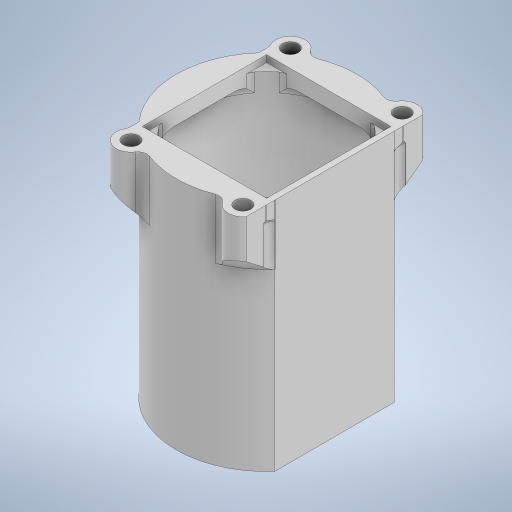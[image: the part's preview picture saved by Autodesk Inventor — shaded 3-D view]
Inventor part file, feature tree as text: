
AUTODESK INVENTOR PART (.ipt)
format: ipt  version: 2024 (Build 280153000, 153)  size: 606,720 bytes
history: native  units: in
note: dims shown in document units (in); Inventor stores cm internally (conversion verified against a paired STEP export)
features: extrude x12, projected_geometry x7, sketch x6, fillet x4, chamfer x1
ambient origin geometry x8: Origin, YZ Plane, XZ Plane, XY Plane, X Axis, Y Axis, Z Axis, Center Point
bodies: Solid1 (feature_tree)
feature tree (30):
  extrude  "Extrusion1"  Depth=1.5748in
  extrude  "Extrusion2"  Depth=1.0236in
  extrude  "Extrusion3"  Depth=0.1181in
  sketch  "Sketch4"  dims[d8=1.7106in d9=0.0in d10=0.1378in]
  extrude  "Extrusion4"  Depth=0.1378in
  extrude  "Extrusion5"  Depth=0.9744in
  extrude  "Extrusion6"  Depth=0.4872in
  extrude  "Extrusion7"  Depth=0.6939in
  extrude  "Extrusion8"  Depth=0.2559in
  fillet  "Fillet1"  Radius=1.1811in
  extrude  "Extrusion9"  Depth=0.5906in
  chamfer  "Chamfer1"  Distance=0.5906in
  fillet  "Fillet4"  Radius=0.2362in
  fillet  "Fillet5"  Radius=0.2362in
  fillet  "Fillet6"  Radius=0.0492in
  extrude  "Extrusion10"  Depth=1.3878in
  extrude  "Extrusion11"  Depth=0.0787in TaperAngle=0.0deg
  extrude  "Extrusion12"  Depth=0.0591in TaperAngle=0.0deg
  sketch  "Sketch1"  dims[d0=0.878in d1=1.5748in]
  sketch  "Sketch2"  dims[d2=0.1181in d3=0.0in d4=1.0236in]
  sketch  "Sketch3"  dims[d5=0.1575in d6=0.0in d7=0.1181in]
  projected_geometry  "Projected Loop1"
  projected_geometry  "Projected Loop2"
  sketch  "Sketch5"  dims[d14=1.3878in d15=0.9744in]
  projected_geometry  "Projected Loop3"
  projected_geometry  "Projected Loop4"
  projected_geometry  "Projected Loop5"
  projected_geometry  "Projected Loop6"
  sketch  "Sketch6"  dims[d17=0.9744in d18=0.4872in d19=0.6939in d20=0.2559in d21=1.1811in d22=0.5906in d23=0.5906in d25=0.2362in d26=0.0in d27=0.2362in d28=0.0in d29=0.0492in d30=1.3878in d31=0.0787in d32=0.0in d33=0.0591in d34=0.0in d35=0.0591in d36=0.0in d37=0.0787in d39=0.0394in d40=0.0in d42=0.187in d43=0.0787in d44=45.0deg d45=0.0197in d46=0.0787in d47=0.0787in d48=0.1181in d49=0.0in d50=1.9685in d51=0.0in d52=1.7717in d53=1.9685in d54=0.0in d41=0.0in]
  projected_geometry  "Projected Loop7"
